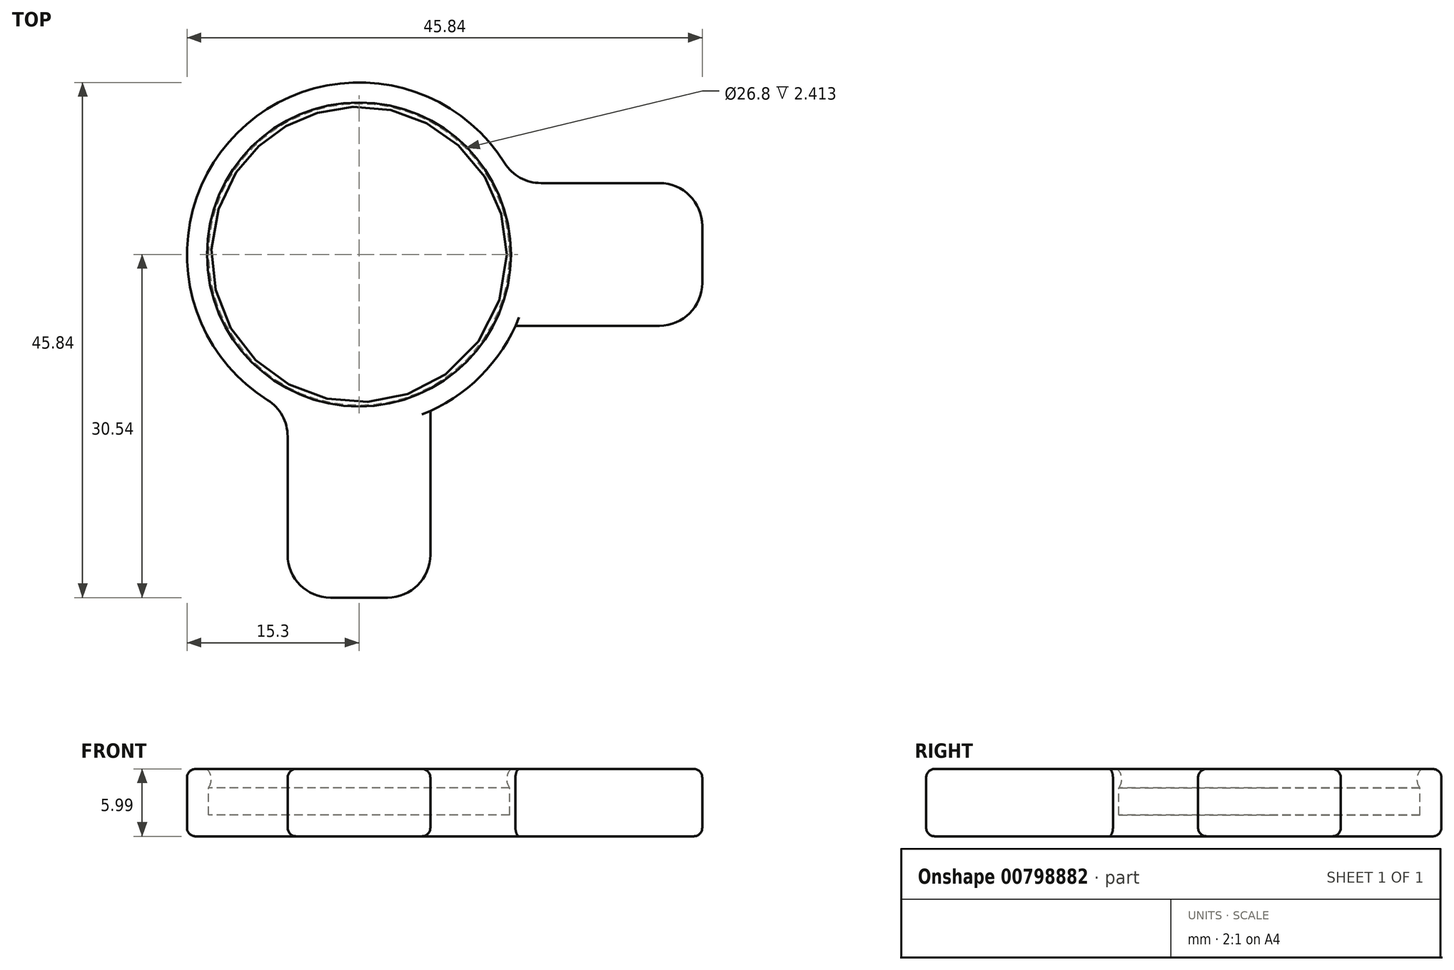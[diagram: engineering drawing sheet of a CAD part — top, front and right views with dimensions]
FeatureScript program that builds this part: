
annotation { "Feature Type Name" : "Feature", "Feature Type Description" : "" }
export const myFeature = defineFeature(function(context is Context, id is Id, definition is map)
    precondition{}
    {
        {
            var Q0;
            Q0=qCreatedBy(makeId("Front.planeOp"),FACE);
            var sketch = newSketch(context, id + "F0", { "sketchPlane" : qUnion([Q0])});
            skLineSegment(sketch, "E0", {"start": v(15.3, 4.17) * mm, "end": v(15.3, 0) * mm});
            skLineSegment(sketch, "E1", {"start": v(15.3, 0) * mm, "end": v(0, 0) * mm});
            skArc(sketch, "E2", {"start": v(15.3, 4.17) * mm, "mid": v(13.5, 4.2) * mm, "end": v(13.53, 5.99) * mm});
            skLineSegment(sketch, "E3", {"start": v(0, 10.9) * mm, "end": v(0, -2.45) * mm, "construction": true});
            skLineSegment(sketch, "E4", {"start": v(0, 0) * mm, "end": v(0, 1.9) * mm});
            skLineSegment(sketch, "E5", {"start": v(0, 1.9) * mm, "end": v(13.4, 1.9) * mm});
            skLineSegment(sketch, "E6", {"start": v(13.4, 1.9) * mm, "end": v(13.4, 4.32) * mm});
            skLineSegment(sketch, "E7", {"start": v(15.3, 4.17) * mm, "end": v(15.3, 5.99) * mm});
            skLineSegment(sketch, "E8", {"start": v(15.3, 5.99) * mm, "end": v(13.53, 5.99) * mm});
            skSolve(sketch);
        }
        {
            var Q0;
            Q0 = qSketchRegion(id + "F0", true);
            var Q1;
            Q1=sQuery(id+"F0.wireOp",EDGE,"E3");
            revolve(context, id + "F1", {"surfaceOperationType" : NewSurfaceOperationType.NEW, "entities" : qUnion([Q0]), "axis" : qUnion([Q1]), "revolveType" : RevolveType.FULL});
        }
        {
            var Q0;
            Q0=makeQuery(id+"F1.opRevolve","SWEPT_FACE",FACE,{"disambiguationData":[OSD([sQuery(id+"F0.wireOp",EDGE,"E8")])]});
            var sketch = newSketch(context, id + "F2", { "sketchPlane" : qUnion([Q0])});
            skLineSegment(sketch, "E9.bottom", {"start": v(30.54, 6.35) * mm, "end": v(13.92, 6.35) * mm});
            skLineSegment(sketch, "E9.top", {"start": v(30.54, -6.35) * mm, "end": v(13.92, -6.35) * mm});
            skLineSegment(sketch, "E9.left", {"start": v(30.54, 6.35) * mm, "end": v(30.54, -6.35) * mm});
            skLineSegment(sketch, "E10.bottom", {"start": v(6.35, -30.54) * mm, "end": v(-6.35, -30.54) * mm});
            skLineSegment(sketch, "E10.left", {"start": v(6.35, -30.54) * mm, "end": v(6.35, -13.92) * mm});
            skLineSegment(sketch, "E10.right", {"start": v(-6.35, -30.54) * mm, "end": v(-6.35, -13.92) * mm});
            skArc(sketch, "E11.0", {"start": v(-6.35, -13.92) * mm, "mid": v(0, -15.3) * mm, "end": v(6.35, -13.92) * mm});
            skArc(sketch, "E12.trimOffspring", {"start": v(13.92, -6.35) * mm, "mid": v(15.3, 0) * mm, "end": v(13.92, 6.35) * mm});
            skSolve(sketch);
        }
        {
            var Q0;
            Q0 = qSketchRegion(id + "F2", true);
            var Q1;
            Q1=makeQuery(id+"F1.opRevolve","SWEPT_FACE",FACE,{"disambiguationData":[OSD([sQuery(id+"F0.wireOp",EDGE,"E1")])]});
            extrude(context, id + "F3", {"entities" : qUnion([Q0]), "operationType" : NewBodyOperationType.ADD, "endBound" : BoundingType.UP_TO_SURFACE, "oppositeDirection" : true, "depth" : 25.4 * mm, "endBoundEntityFace" : qUnion([Q1]), "offsetDistance" : 25.4 * mm});
        }
        {
            var Q0;
            Q0=makeQuery(id+"F3.opExtrude","SWEPT_EDGE",EDGE,{"disambiguationData":[OSD([sQuery(id+"F2.wireOp",EDGE,"E10.bottom"),sQuery(id+"F2.wireOp",EDGE,"E10.right")])]});
            var Q1;
            Q1=makeQuery(id+"F3.opExtrude","SWEPT_EDGE",EDGE,{"disambiguationData":[OSD([sQuery(id+"F0.wireOp",EDGE,"E7"),sQuery(id+"F0.wireOp",EDGE,"E8"),sQuery(id+"F2.wireOp",EDGE,"E10.right"),sQuery(id+"F2.wireOp",EDGE,"E11.0")])]});
            var Q2;
            Q2=makeQuery(id+"F3.opExtrude","SWEPT_EDGE",EDGE,{"disambiguationData":[OSD([sQuery(id+"F2.wireOp",EDGE,"E10.bottom"),sQuery(id+"F2.wireOp",EDGE,"E10.left")])]});
            var Q3;
            Q3=makeQuery(id+"F3.opExtrude","SWEPT_EDGE",EDGE,{"disambiguationData":[OSD([sQuery(id+"F0.wireOp",EDGE,"E7"),sQuery(id+"F0.wireOp",EDGE,"E8"),sQuery(id+"F2.wireOp",EDGE,"E10.left"),sQuery(id+"F2.wireOp",EDGE,"E11.0")])]});
            var Q4;
            Q4=makeQuery(id+"F3.opExtrude","SWEPT_EDGE",EDGE,{"disambiguationData":[OSD([sQuery(id+"F0.wireOp",EDGE,"E7"),sQuery(id+"F0.wireOp",EDGE,"E8"),sQuery(id+"F2.wireOp",EDGE,"E9.top"),sQuery(id+"F2.wireOp",EDGE,"E12.trimOffspring")])]});
            var Q5;
            Q5=makeQuery(id+"F3.opExtrude","SWEPT_EDGE",EDGE,{"disambiguationData":[OSD([sQuery(id+"F2.wireOp",EDGE,"E9.top"),sQuery(id+"F2.wireOp",EDGE,"E9.left")])]});
            var Q6;
            Q6=makeQuery(id+"F3.opExtrude","SWEPT_EDGE",EDGE,{"disambiguationData":[OSD([sQuery(id+"F2.wireOp",EDGE,"E9.bottom"),sQuery(id+"F2.wireOp",EDGE,"E9.left")])]});
            var Q7;
            Q7=makeQuery(id+"F3.opExtrude","SWEPT_EDGE",EDGE,{"disambiguationData":[OSD([sQuery(id+"F0.wireOp",EDGE,"E7"),sQuery(id+"F0.wireOp",EDGE,"E8"),sQuery(id+"F2.wireOp",EDGE,"E9.bottom"),sQuery(id+"F2.wireOp",EDGE,"E12.trimOffspring")])]});
            fillet(context, id + "F4", {"entities" : qUnion([Q0, Q1, Q2, Q3, Q4, Q5, Q6, Q7]), "radius" : 3.8 * mm, "tangentPropagation" : true, "allowEdgeOverflow" : false});
        }
        {
            var Q0;
            Q0=makeQuery(id+"F3.opExtrude","CAP_EDGE",EDGE,{"disambiguationData":[OSD([sQuery(id+"F2.wireOp",EDGE,"E10.bottom")])],"isStart":true});
            var Q1;
            Q1=makeQuery(id+"F3.opExtrude","CAP_EDGE",EDGE,{"disambiguationData":[OSD([sQuery(id+"F2.wireOp",EDGE,"E10.bottom")])],"isStart":false});
            fillet(context, id + "F5", {"entities" : qUnion([Q0, Q1]), "radius" : 0.76 * mm, "tangentPropagation" : true, "allowEdgeOverflow" : false});
        }
    });
